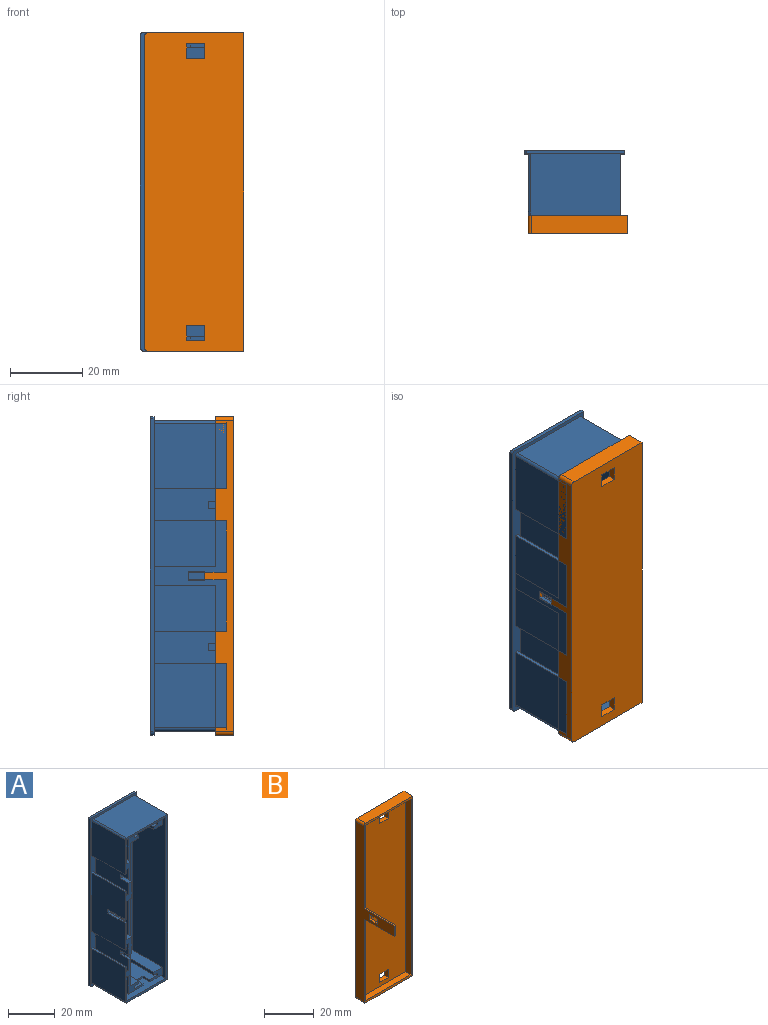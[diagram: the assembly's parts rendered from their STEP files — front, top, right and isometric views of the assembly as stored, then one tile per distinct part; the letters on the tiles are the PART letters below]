
ASSEMBLY  parts=2 mates=1
PART A: 101 faces, bbox 27.7x21x88.2 mm
  f0: plane 8.75x2mm, normal (1,0,0), area 17.5mm2, adj f39,f71,f80,f97
  f1: plane 86x25.5mm, normal (0,-1,0), area 193.1mm2, adj f3,f10,f53,f54,f55,f56,f57,f58
  f2: plane 17.75x4mm, normal (0,-1,0), area 34.5mm2, adj f4,f9,f52,f72,f73,f74,f75,f76
  f3: plane 20x3mm, normal (0,0,1), area 55mm2, adj f1,f14,f15,f69,f98,f100
  f4: plane 20x20mm, normal (1,0,0), area 324mm2, adj f2,f5,f8,f71,f75,f76,f79,f80
  f5: plane 7.5x3mm, normal (0,-1,0), area 22.5mm2, adj f4,f6,f75,f91
  f6: plane 20x18mm, normal (-1,0,0), area 275mm2, adj f5,f8,f39,f75,f80,f90,f91,f92
  f7: plane 88.2x27.7mm, normal (0,-1,0), area 296.1mm2, adj f9,f10,f11,f16,f17,f18,f19,f20
  f8: plane 7.5x3mm, normal (0,-1,0), area 22.5mm2, adj f4,f6,f80,f90
  f9: plane 20x1mm, normal (0,0,-1), area 20mm2, adj f2,f7,f74,f84
  f10: plane 20x1mm, normal (0,0,-1), area 20mm2, adj f1,f7,f68,f83
  f11: plane 20x1mm, normal (0,0,1), area 20mm2, adj f7,f71,f77,f83
  f12: plane 23.5x12.5mm, normal (0,-1,0), area 58mm2, adj f30,f31,f53,f54,f55,f56
  f13: plane 80x19.5mm, normal (0,-1,0), area 1514.2mm2, adj f23,f24,f25,f26,f27,f33,f34,f35
  f14: plane 22.25x18mm, normal (-1,0,0), area 239.2mm2, adj f3,f15,f29,f39,f97,f100
  f15: plane 23.5x12.5mm, normal (0,-1,0), area 58mm2, adj f3,f14,f29,f53,f69,f70
  f16: plane 86.55x1mm, normal (-1,0,0), area 86.5mm2, adj f7,f17,f21,f22
  f17: cylinder r=1.1mm len=1.1mm, axis (0,1,0), area 1.7mm2, adj f7,f16,f18,f22
  f18: plane 26.6x1mm, normal (0,0,-1), area 26.6mm2, adj f7,f17,f19,f22
  f19: plane 88.2x1mm, normal (1,0,0), area 88.2mm2, adj f7,f18,f20,f22
  f20: plane 27.15x1mm, normal (0,0,1), area 27.1mm2, adj f7,f19,f21,f22
  f21: cylinder r=1.23mm len=1mm, axis (0,1,0), area 0.8mm2, adj f7,f16,f20,f22
  f22: plane 88.2x27.7mm, normal (0,1,0), area 2442.8mm2, adj f16,f17,f18,f19,f20,f21
  f23: plane 18x5.25mm, normal (0,0,-1), area 94.5mm2, adj f13,f24,f38,f39
  f24: plane 18x1.5mm, normal (1,0,0), area 27mm2, adj f13,f23,f25,f39
  f25: plane 18x2.5mm, normal (0,0,1), area 45mm2, adj f13,f24,f26,f39
  f26: plane 18x1.3mm, normal (1,0,0), area 23.4mm2, adj f13,f25,f27,f39
  f27: plane 18x14mm, normal (0,0,-1), area 236mm2, adj f13,f26,f28,f39,f42,f43,f45,f81
  f28: plane 4x1mm, normal (1,0,0), area 4mm2, adj f27,f29,f39,f81
  f29: plane 20.5x18mm, normal (0,0,1), area 353mm2, adj f14,f15,f28,f39,f42,f45,f53,f81
  f30: plane 22.25x18mm, normal (-1,0,0), area 239.3mm2, adj f12,f31,f39,f56,f95,f96
  f31: plane 20.5x18mm, normal (0,0,-1), area 353mm2, adj f12,f30,f32,f39,f46,f51,f53,f82
  f32: plane 4x1mm, normal (1,0,0), area 4mm2, adj f31,f33,f39,f82
  f33: plane 18x14mm, normal (0,0,1), area 236mm2, adj f13,f32,f34,f39,f46,f50,f51,f82
  f34: plane 18x1.3mm, normal (1,0,0), area 23.4mm2, adj f13,f33,f35,f39
  f35: plane 18x2.5mm, normal (0,0,-1), area 45mm2, adj f13,f34,f36,f39
  f36: plane 18x1.5mm, normal (1,0,0), area 27mm2, adj f13,f35,f37,f39
  f37: plane 18x5.25mm, normal (0,0,1), area 94.5mm2, adj f13,f36,f38,f39
  f38: plane 74.4x18mm, normal (1,0,0), area 1339.2mm2, adj f13,f23,f37,f39
  f39: plane 82x8.75mm, normal (0,-1,0), area 120.4mm2, adj f0,f6,f14,f23,f24,f25,f26,f27
  f40: plane 18x1.5mm, normal (-1,0,0), area 27mm2, adj f13,f41,f44,f45
  f41: plane 18x5.25mm, normal (0,0,-1), area 94.5mm2, adj f13,f40,f45,f53
  f42: plane 4x1mm, normal (-1,0,0), area 4mm2, adj f27,f29,f45,f81
  f43: plane 18x1.3mm, normal (-1,0,0), area 23.4mm2, adj f13,f27,f44,f45
  f44: plane 18x2.5mm, normal (0,0,1), area 45mm2, adj f13,f40,f43,f45
  f45: plane 7.75x3.8mm, normal (0,-1,0), area 19.2mm2, adj f27,f29,f40,f41,f42,f43,f44,f53
  f46: plane 4x1mm, normal (-1,0,0), area 4mm2, adj f31,f33,f51,f82
  f47: plane 18x5.25mm, normal (0,0,1), area 94.5mm2, adj f13,f48,f51,f53
  f48: plane 18x1.5mm, normal (-1,0,0), area 27mm2, adj f13,f47,f49,f51
  f49: plane 18x2.5mm, normal (0,0,-1), area 45mm2, adj f13,f48,f50,f51
  f50: plane 18x1.3mm, normal (-1,0,0), area 23.4mm2, adj f13,f33,f49,f51
  f51: plane 7.75x3.8mm, normal (0,-1,0), area 19.2mm2, adj f31,f33,f46,f47,f48,f49,f50,f53
  f52: plane 8.75x2mm, normal (1,0,0), area 17.5mm2, adj f2,f39,f75,f95
  f53: plane 84x20mm, normal (-1,0,0), area 1543.2mm2, adj f1,f12,f13,f15,f29,f31,f41,f45
  f54: plane 23.5x20mm, normal (0,0,1), area 470mm2, adj f1,f12,f53,f55
  f55: plane 20x12.5mm, normal (1,0,0), area 250mm2, adj f1,f12,f54,f56
  f56: plane 20x3mm, normal (0,0,-1), area 55mm2, adj f1,f12,f30,f55,f94,f96
  f57: plane 20x1mm, normal (0,0,1), area 20mm2, adj f1,f7,f58,f84
  f58: plane 20x2.5mm, normal (1,0,0), area 50mm2, adj f1,f7,f57,f59
  f59: plane 20x1mm, normal (0,0,1), area 20mm2, adj f1,f7,f58,f60
  f60: plane 20x17.75mm, normal (-1,0,0), area 355mm2, adj f1,f7,f59,f61
  f61: cylinder r=1mm len=20mm, axis (0,1,0), area 31.4mm2, adj f1,f7,f60,f62
  f62: plane 24.5x20mm, normal (0,0,-1), area 490mm2, adj f1,f7,f61,f63
  f63: plane 86x20mm, normal (1,0,0), area 1720mm2, adj f1,f7,f62,f64
  f64: plane 24.83x20mm, normal (0,0,1), area 496.6mm2, adj f1,f7,f63,f65
  f65: cylinder r=1.05mm len=20mm, axis (0,1,0), area 19.6mm2, adj f1,f7,f64,f66
  f66: plane 20x18.08mm, normal (-1,0,0), area 361.6mm2, adj f1,f7,f65,f67
  f67: plane 20x1mm, normal (0,0,-1), area 20mm2, adj f1,f7,f66,f68
  f68: plane 20x2.5mm, normal (1,0,0), area 50mm2, adj f1,f7,f10,f67
  f69: plane 20x12.5mm, normal (1,0,0), area 250mm2, adj f1,f3,f15,f70
  f70: plane 23.5x20mm, normal (0,0,-1), area 470mm2, adj f1,f15,f53,f69
  f71: plane 17.75x4mm, normal (0,-1,0), area 34.5mm2, adj f0,f4,f11,f72,f77,f78,f79,f80
  f72: plane 30.5x20mm, normal (-1,0,0), area 589mm2, adj f2,f7,f71,f73,f76,f78,f79,f85
  f73: plane 20x1mm, normal (0,0,-1), area 20mm2, adj f2,f7,f72,f74
  f74: plane 20x2.5mm, normal (1,0,0), area 50mm2, adj f2,f7,f9,f73
  f75: plane 20x3mm, normal (0,0,1), area 60mm2, adj f2,f4,f5,f6,f52
  f76: plane 10.5x1mm, normal (0,0,1), area 10.5mm2, adj f2,f4,f72,f85
  f77: plane 20x2.5mm, normal (1,0,0), area 50mm2, adj f7,f11,f71,f78
  f78: plane 20x1mm, normal (0,0,1), area 20mm2, adj f7,f71,f72,f77
  f79: plane 10.5x1mm, normal (0,0,-1), area 10.5mm2, adj f4,f71,f72,f85
  f80: plane 20x3mm, normal (0,0,-1), area 60mm2, adj f0,f4,f6,f8,f71
  f81: plane 4x1mm, normal (0,-1,0), area 4mm2, adj f27,f28,f29,f42
  f82: plane 4x1mm, normal (0,-1,0), area 4mm2, adj f31,f32,f33,f46
  f83: plane 20x14mm, normal (-1,0,0), area 270mm2, adj f1,f7,f10,f11,f71,f97,f99,f100
  f84: plane 20x14mm, normal (-1,0,0), area 270mm2, adj f1,f2,f7,f9,f57,f93,f95,f96
  f85: plane 2x1mm, normal (0,-1,0), area 2mm2, adj f4,f72,f76,f79
  f86: plane 3x1mm, normal (0,-1,0), area 3mm2, adj f4,f87,f88,f89
  f87: plane 10x1mm, normal (0,0,-1), area 10mm2, adj f4,f86,f88,f92
  f88: plane 10x3mm, normal (-1,0,0), area 30mm2, adj f86,f87,f89,f92
  f89: plane 10x1mm, normal (0,0,1), area 10mm2, adj f4,f86,f88,f92
  f90: plane 17x3mm, normal (0,0,1), area 51mm2, adj f4,f6,f8,f92
  f91: plane 17x3mm, normal (0,0,-1), area 51mm2, adj f4,f5,f6,f92
  f92: plane 5x3mm, normal (0,-1,0), area 12mm2, adj f4,f6,f87,f88,f89,f90,f91
  f93: plane 5x1mm, normal (0,0,1), area 5mm2, adj f1,f84,f94,f96
  f94: plane 8.75x5mm, normal (1,0,0), area 43.8mm2, adj f1,f56,f93,f96
  f95: plane 5x2mm, normal (0,0,-1), area 10mm2, adj f2,f30,f52,f84,f96
  f96: plane 10.75x2mm, normal (0,-1,0), area 12.8mm2, adj f30,f56,f84,f93,f94,f95
  f97: plane 5x2mm, normal (0,0,1), area 10mm2, adj f0,f14,f71,f83,f100
  f98: plane 8.75x5mm, normal (1,0,0), area 43.8mm2, adj f1,f3,f99,f100
  f99: plane 5x1mm, normal (0,0,-1), area 5mm2, adj f1,f83,f98,f100
  f100: plane 10.75x2mm, normal (0,-1,0), area 12.8mm2, adj f3,f14,f83,f97,f98,f99
PART B: 28 faces, bbox 27.6x22x88.1 mm
  f0: plane 86.1x22mm, normal (-1,0,0), area 505.9mm2, adj f3,f4,f16,f20,f21,f22,f23,f24
  f1: plane 86.1x20mm, normal (1,0,0), area 333.7mm2, adj f2,f17,f19,f20,f21,f22,f23,f24
  f2: plane 86.1x25.6mm, normal (0,-1,0), area 2164.2mm2, adj f1,f7,f8,f9,f10,f11,f12,f13
  f3: cylinder r=1mm len=5mm, axis (0,1,0), area 7.9mm2, adj f0,f15,f16,f20
  f4: cylinder r=1mm len=5mm, axis (0,1,0), area 7.9mm2, adj f0,f5,f16,f20
  f5: plane 26.6x5mm, normal (0,0,-1), area 133mm2, adj f4,f6,f16,f20
  f6: plane 88.1x5mm, normal (1,0,0), area 440.5mm2, adj f5,f15,f16,f20
  f7: plane 4x2mm, normal (1,0,0), area 8mm2, adj f2,f8,f13,f16
  f8: plane 5x2mm, normal (0,0,-1), area 10mm2, adj f2,f7,f9,f16
  f9: plane 4x2mm, normal (-1,0,0), area 8mm2, adj f2,f8,f13,f16
  f10: plane 5x2mm, normal (0,0,1), area 10mm2, adj f2,f11,f14,f16
  f11: plane 4x2mm, normal (1,0,0), area 8mm2, adj f2,f10,f12,f16
  f12: plane 5x2mm, normal (0,0,-1), area 10mm2, adj f2,f11,f14,f16
  f13: plane 5x2mm, normal (0,0,1), area 10mm2, adj f2,f7,f9,f16
  f14: plane 4x2mm, normal (-1,0,0), area 8mm2, adj f2,f10,f12,f16
  f15: plane 26.6x5mm, normal (0,0,1), area 133mm2, adj f3,f6,f16,f20
  f16: plane 88.1x27.6mm, normal (0,1,0), area 2391.1mm2, adj f0,f3,f4,f5,f6,f7,f8,f9
  f17: plane 25.6x3mm, normal (0,0,-1), area 76.8mm2, adj f1,f2,f18,f20
  f18: plane 86.1x3mm, normal (-1,0,0), area 258.3mm2, adj f2,f17,f19,f20
  f19: plane 25.6x3mm, normal (0,0,1), area 76.8mm2, adj f1,f2,f18,f20
  f20: plane 88.1x27.6mm, normal (0,-1,0), area 221.9mm2, adj f0,f1,f3,f4,f5,f6,f15,f17
  f21: plane 17x1mm, normal (0,0,1), area 17mm2, adj f0,f1,f20,f23
  f22: plane 17x1mm, normal (0,0,-1), area 17mm2, adj f0,f1,f20,f23
  f23: plane 5.1x1mm, normal (0,-1,0), area 5.1mm2, adj f0,f1,f21,f22
  f24: plane 4.5x1mm, normal (0,0,-1), area 4.5mm2, adj f0,f1,f25,f27
  f25: plane 2.5x1mm, normal (0,-1,0), area 2.5mm2, adj f0,f1,f24,f26
  f26: plane 4.5x1mm, normal (0,0,1), area 4.5mm2, adj f0,f1,f25,f27
  f27: plane 2.5x1mm, normal (0,1,0), area 2.5mm2, adj f0,f1,f24,f26
PLACE A t=(38.93,18.85,4.89)mm
PLACE B rot(axis=(1,0,0),180deg) t=(-6.57,-4.15,88.94)mm
MATE fastened A.f72 <-> B.f0  axis (-1,0,0) through (-6.57,8.35,44.89)mm
